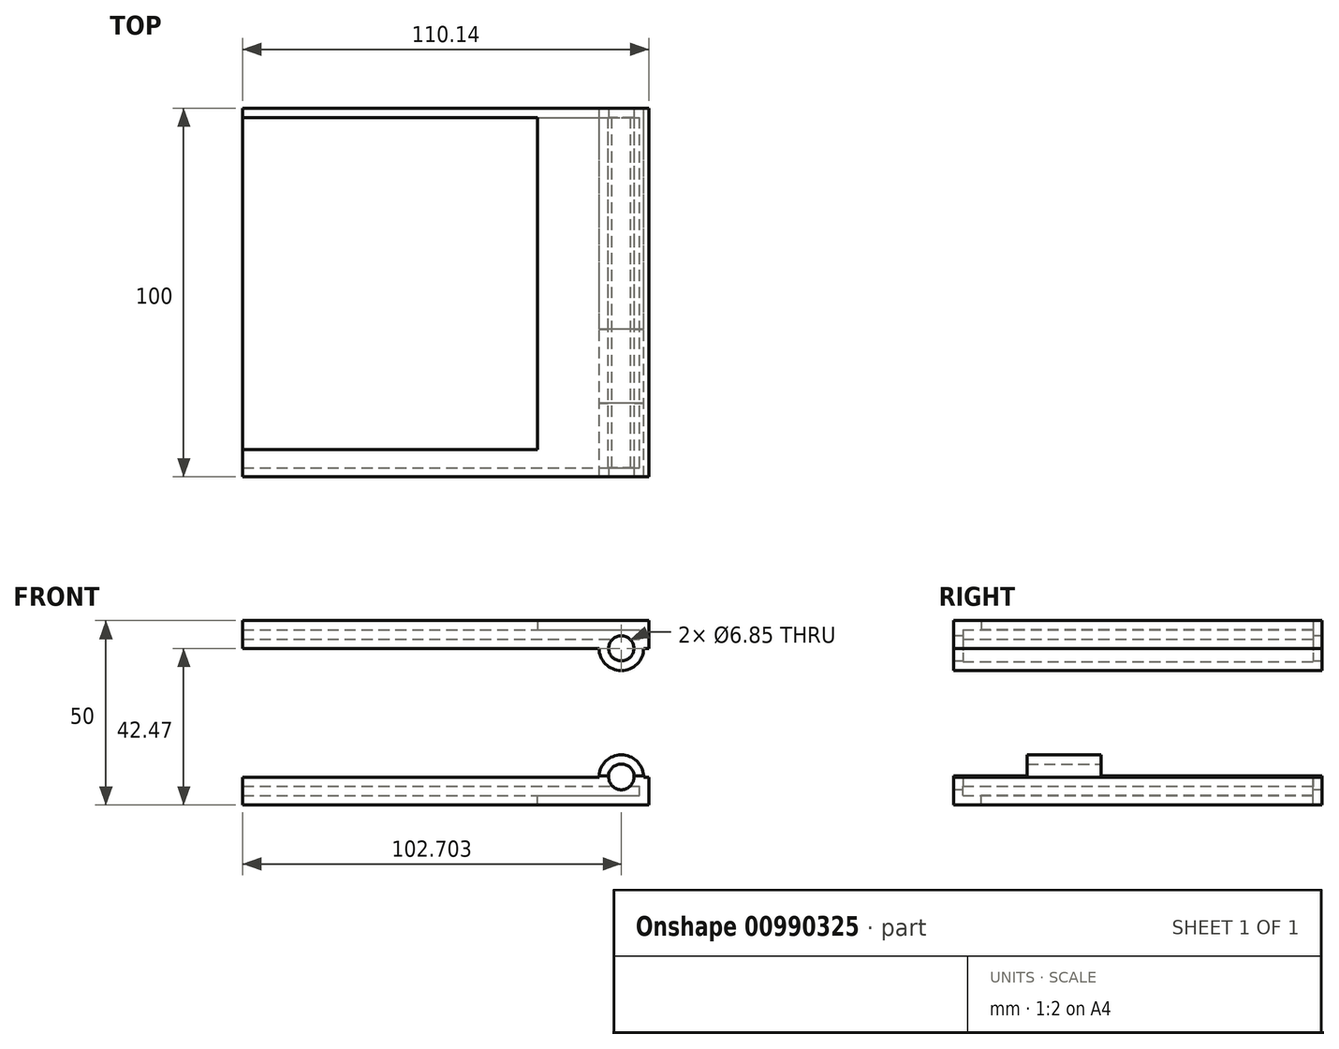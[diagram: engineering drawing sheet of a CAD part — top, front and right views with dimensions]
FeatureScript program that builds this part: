
annotation { "Feature Type Name" : "Feature", "Feature Type Description" : "" }
export const myFeature = defineFeature(function(context is Context, id is Id, definition is map)
    precondition{}
    {
        {
            var Q0;
            Q0=qCreatedBy(makeId("Front.planeOp"),FACE);
            var sketch = newSketch(context, id + "F0", { "sketchPlane" : qUnion([Q0])});
            skLineSegment(sketch, "E0.bottom", {"start": v(-48.54, 0) * mm, "end": v(61.6, 0) * mm});
            skLineSegment(sketch, "E0.top", {"start": v(-48.54, 7.53) * mm, "end": v(48.12, 7.53) * mm});
            skLineSegment(sketch, "E0.left", {"start": v(-48.54, 0) * mm, "end": v(-48.54, 7.53) * mm});
            skLineSegment(sketch, "E0.right", {"start": v(61.6, 0) * mm, "end": v(61.6, 7.53) * mm});
            skArc(sketch, "E1", {"start": v(60.2, 7.53) * mm, "mid": v(54.16, 13.57) * mm, "end": v(48.12, 7.53) * mm});
            skLineSegment(sketch, "E2.trimOffspring", {"start": v(60.2, 7.53) * mm, "end": v(61.6, 7.53) * mm});
            skSolve(sketch);
        }
        {
            var Q0;
            Q0=makeQuery(id+"F0.imprint","IMPRINT",FACE,{"disambiguationData":[TD([[makeQuery(id+"F0.imprint","IMPRINT",EDGE,{"derivedFrom":sQuery(id+"F0.wireOp",EDGE,"E0.bottom")}),1.0]])]});
            extrude(context, id + "F1", {"entities" : qUnion([Q0]), "depth" : 50 * mm, "offsetDistance" : 25 * mm, "hasSecondDirection" : true, "secondDirectionOppositeDirection" : true, "secondDirectionDepth" : 50 * mm});
        }
        {
            var Q0;
            Q0=makeQuery(id+"F1.opExtrude","SWEPT_FACE",FACE,{"disambiguationData":[OSD([sQuery(id+"F0.wireOp",EDGE,"E0.left")])]});
            shell(context, id + "F2", {"entities" : qUnion([Q0]), "thickness" : 2.5 * mm});
        }
        {
            var Q0;
            Q0=makeQuery(id+"F1.opExtrude","SWEPT_FACE",FACE,{"disambiguationData":[OSD([sQuery(id+"F0.wireOp",EDGE,"E0.left")])]});
            var sketch = newSketch(context, id + "F3", { "sketchPlane" : qUnion([Q0])});
            skLineSegment(sketch, "E3.bottom", {"start": v(-47.5, 0) * mm, "end": v(42.55, 0) * mm});
            skLineSegment(sketch, "E3.top", {"start": v(-47.5, 5.03) * mm, "end": v(42.55, 5.03) * mm});
            skLineSegment(sketch, "E3.left", {"start": v(-47.5, 0) * mm, "end": v(-47.5, 5.03) * mm});
            skLineSegment(sketch, "E3.right", {"start": v(42.55, 0) * mm, "end": v(42.55, 5.03) * mm});
            skSolve(sketch);
        }
        {
            var Q0;
            Q0 = qSketchRegion(id + "F3", true);
            extrude(context, id + "F4", {"entities" : qUnion([Q0]), "operationType" : NewBodyOperationType.REMOVE, "oppositeDirection" : true, "depth" : 80 * mm, "offsetDistance" : 25 * mm});
        }
        {
            var Q0;
            Q0=makeQuery(id+"F1.opExtrude","CAP_FACE",FACE,{"disambiguationData":[OSD([sQuery(id+"F0.wireOp",EDGE,"E0.bottom"),sQuery(id+"F0.wireOp",EDGE,"E0.top"),sQuery(id+"F0.wireOp",EDGE,"E0.left"),sQuery(id+"F0.wireOp",EDGE,"E0.right"),sQuery(id+"F0.wireOp",EDGE,"E1"),sQuery(id+"F0.wireOp",EDGE,"E2.trimOffspring")])],"isStart":false});
            var sketch = newSketch(context, id + "F5", { "sketchPlane" : qUnion([Q0])});
            skCircle(sketch, "E4", {"center": v(54.16, 7.53) * mm, "radius": 3.42 * mm});
            skSolve(sketch);
        }
        {
            var Q0;
            Q0=makeQuery(id+"F5.imprint","IMPRINT",FACE,{"disambiguationData":[TD([[makeQuery(id+"F5.imprint","IMPRINT",EDGE,{"derivedFrom":sQuery(id+"F5.wireOp",EDGE,"E4")}),1.0]])]});
            extrude(context, id + "F6", {"entities" : qUnion([Q0]), "operationType" : NewBodyOperationType.REMOVE, "oppositeDirection" : true, "depth" : 154.5 * mm, "offsetDistance" : 25 * mm});
        }
        {
            var Q0;
            Q0=qCreatedBy(makeId("Top.planeOp"),FACE);
            cPlane(context, id + "F7", {"entities" : qUnion([Q0]), "cplaneType" : CPlaneType.OFFSET, "offset" : 25 * mm, "width" : 150 * mm, "height" : 150 * mm});
        }
        {
            var Q0;
            Q0=makeQuery(id+"F1.opExtrude","SWEPT_BODY",BODY,{"disambiguationData":[OSD([sQuery(id+"F0.wireOp",EDGE,"E0.bottom"),sQuery(id+"F0.wireOp",EDGE,"E0.top"),sQuery(id+"F0.wireOp",EDGE,"E0.left"),sQuery(id+"F0.wireOp",EDGE,"E0.right"),sQuery(id+"F0.wireOp",EDGE,"E1"),sQuery(id+"F0.wireOp",EDGE,"E2.trimOffspring")])]});
            var Q1;
            Q1=qCreatedBy(id+"F7.planeOp",FACE);
            mirror(context, id + "F8", {"entities" : qUnion([Q0]), "mirrorPlane" : qUnion([Q1])});
        }
        {
            var Q0;
            Q0=qCreatedBy(id+"F7.planeOp",FACE);
            var sketch = newSketch(context, id + "F9", { "sketchPlane" : qUnion([Q0])});
            skLineSegment(sketch, "E5.bottom", {"start": v(48.12, -50) * mm, "end": v(64.87, -50) * mm});
            skLineSegment(sketch, "E5.top", {"start": v(48.12, 50) * mm, "end": v(64.87, 50) * mm});
            skLineSegment(sketch, "E5.left", {"start": v(48.12, -50) * mm, "end": v(48.12, 50) * mm});
            skLineSegment(sketch, "E5.right", {"start": v(64.87, -50) * mm, "end": v(64.87, 50) * mm});
            skLineSegment(sketch, "E6", {"start": v(48.12, -30) * mm, "end": v(64.87, -30) * mm});
            skLineSegment(sketch, "E7", {"start": v(48.12, -10) * mm, "end": v(64.87, -10) * mm});
            skSolve(sketch);
        }
        {
            var Q0;
            {var subQ0=sQuery(id+"F9.wireOp",EDGE,"E5.bottom");Q0=makeQuery(id+"F9.imprint","IMPRINT",FACE,{"disambiguationData":[TD([[makeQuery(id+"F9.imprint","IMPRINT",EDGE,{"derivedFrom":subQ0}),1.0]])]});}
            var Q1;
            {var subQ0=sQuery(id+"F9.wireOp",EDGE,"E5.top");Q1=makeQuery(id+"F9.imprint","IMPRINT",FACE,{"disambiguationData":[TD([[makeQuery(id+"F9.imprint","IMPRINT",EDGE,{"derivedFrom":subQ0}),-1.0]])]});}
            extrude(context, id + "F10", {"entities" : qUnion([Q0, Q1]), "operationType" : NewBodyOperationType.REMOVE, "oppositeDirection" : true, "depth" : 17.1 * mm, "offsetDistance" : 25 * mm});
        }
    });
